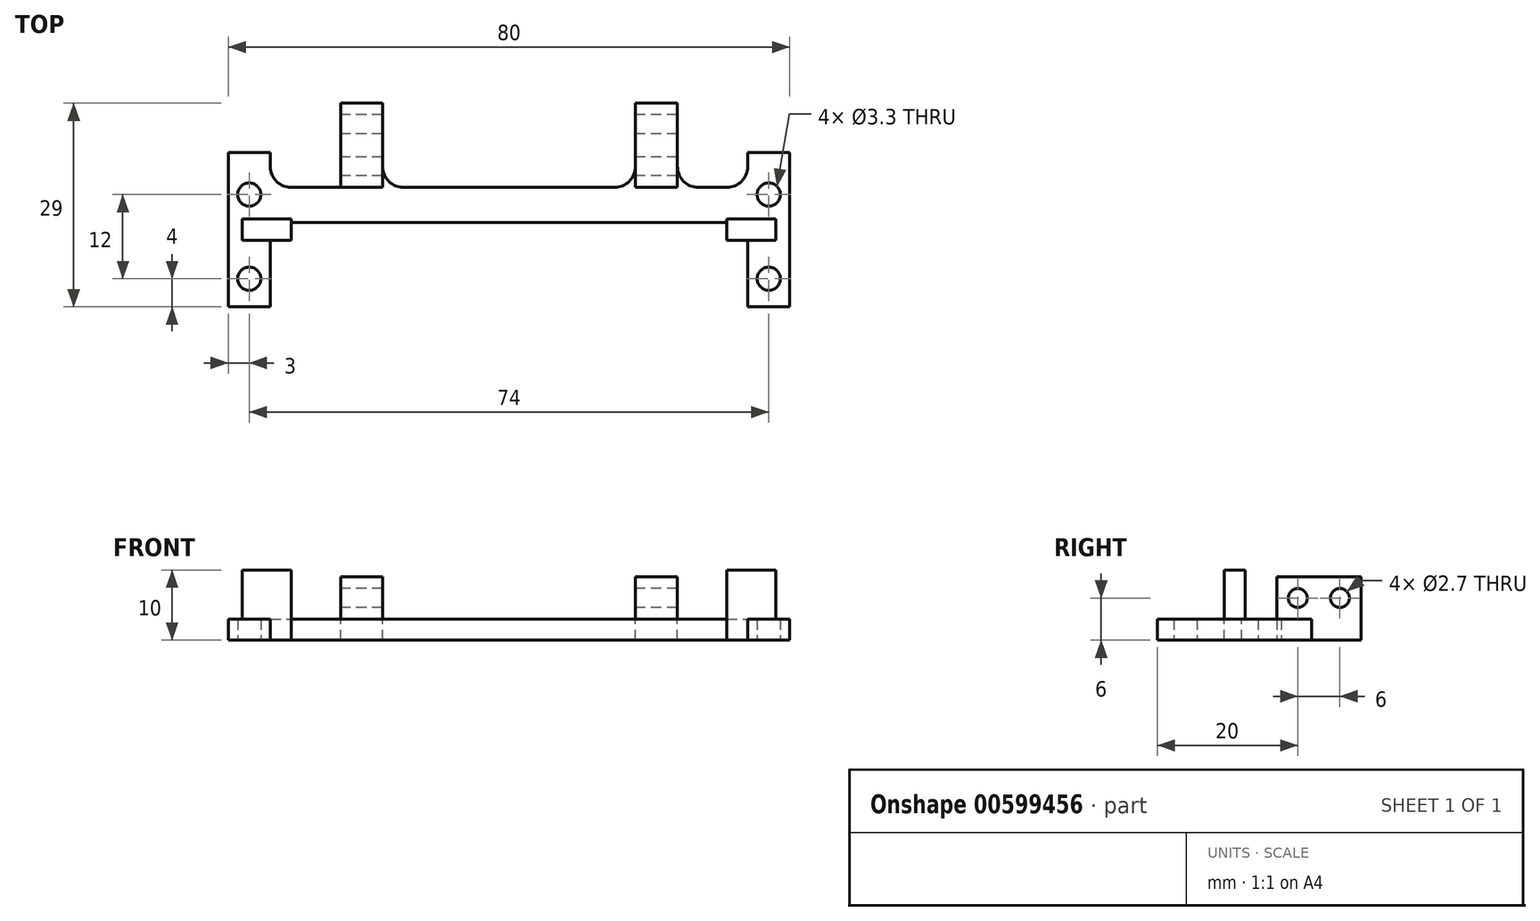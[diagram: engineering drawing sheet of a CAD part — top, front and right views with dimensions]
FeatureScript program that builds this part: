
annotation { "Feature Type Name" : "Feature", "Feature Type Description" : "" }
export const myFeature = defineFeature(function(context is Context, id is Id, definition is map)
    precondition{}
    {
        {
            var Q0;
            Q0=qCreatedBy(makeId("Top.planeOp"),FACE);
            var sketch = newSketch(context, id + "F0", { "sketchPlane" : qUnion([Q0])});
            skLineSegment(sketch, "E0.bottom", {"start": v(-40, 6) * mm, "end": v(-34, 6) * mm});
            skLineSegment(sketch, "E0.top", {"start": v(-34, -4) * mm, "end": v(34, -4) * mm});
            skLineSegment(sketch, "E0.left", {"start": v(-40, 6) * mm, "end": v(-40, -4) * mm});
            skLineSegment(sketch, "E0.right", {"start": v(40, 6) * mm, "end": v(40, -4) * mm});
            skCircle(sketch, "E1", {"center": v(-37, 0) * mm, "radius": 1.65 * mm});
            skCircle(sketch, "E2", {"center": v(37, 0) * mm, "radius": 1.65 * mm});
            skLineSegment(sketch, "E3", {"start": v(34, 6) * mm, "end": v(34, 1) * mm});
            skLineSegment(sketch, "E4", {"start": v(-34, 6) * mm, "end": v(-34, 1) * mm});
            skLineSegment(sketch, "E5", {"start": v(-34, 1) * mm, "end": v(34, 1) * mm});
            skLineSegment(sketch, "E6.trimOffspring", {"start": v(34, 6) * mm, "end": v(40, 6) * mm});
            skLineSegment(sketch, "E7.top", {"start": v(34, -16) * mm, "end": v(40, -16) * mm});
            skLineSegment(sketch, "E7.right", {"start": v(40, -4) * mm, "end": v(40, -16) * mm});
            skLineSegment(sketch, "E8.trimOffspring", {"start": v(34, -4) * mm, "end": v(34, -16) * mm});
            skLineSegment(sketch, "E9.MirrorCS", {"start": v(-34, -4) * mm, "end": v(-34, -16) * mm});
            skLineSegment(sketch, "E10.MirrorCS", {"start": v(-34, -16) * mm, "end": v(-40, -16) * mm});
            skLineSegment(sketch, "E11.MirrorCS", {"start": v(-40, -4) * mm, "end": v(-40, -16) * mm});
            skCircle(sketch, "E12", {"center": v(-37, -12) * mm, "radius": 1.65 * mm});
            skCircle(sketch, "E13.MirrorC", {"center": v(37, -12) * mm, "radius": 1.65 * mm});
            skSolve(sketch);
        }
        {
            var Q0;
            Q0=makeQuery(id+"F0.imprint","IMPRINT",FACE,{"disambiguationData":[TD([[makeQuery(id+"F0.imprint","IMPRINT",EDGE,{"derivedFrom":sQuery(id+"F0.wireOp",EDGE,"E0.bottom")}),-1.0]])]});
            extrude(context, id + "F1", {"entities" : qUnion([Q0]), "depth" : 3 * mm, "offsetDistance" : 25 * mm});
        }
        {
            var Q0;
            Q0=makeQuery(id+"F1.opExtrude","CAP_FACE",FACE,{"disambiguationData":[OSD([sQuery(id+"F0.wireOp",EDGE,"E0.bottom"),sQuery(id+"F0.wireOp",EDGE,"E0.top"),sQuery(id+"F0.wireOp",EDGE,"E0.left"),sQuery(id+"F0.wireOp",EDGE,"E0.right"),sQuery(id+"F0.wireOp",EDGE,"E1"),sQuery(id+"F0.wireOp",EDGE,"E2"),sQuery(id+"F0.wireOp",EDGE,"E3"),sQuery(id+"F0.wireOp",EDGE,"E4"),sQuery(id+"F0.wireOp",EDGE,"E5"),sQuery(id+"F0.wireOp",EDGE,"E6.trimOffspring")])],"isStart":false});
            var sketch = newSketch(context, id + "F2", { "sketchPlane" : qUnion([Q0])});
            skLineSegment(sketch, "E14.bottom", {"start": v(-24, 13) * mm, "end": v(-18, 13) * mm});
            skLineSegment(sketch, "E14.top", {"start": v(-24, -4) * mm, "end": v(-18, -4) * mm});
            skLineSegment(sketch, "E14.left", {"start": v(-24, 13) * mm, "end": v(-24, -4) * mm});
            skLineSegment(sketch, "E14.right", {"start": v(-18, 13) * mm, "end": v(-18, -4) * mm});
            skLineSegment(sketch, "E15.MirrorCS", {"start": v(18, 13) * mm, "end": v(18, -4) * mm});
            skLineSegment(sketch, "E16.MirrorCS", {"start": v(24, 13) * mm, "end": v(18, 13) * mm});
            skLineSegment(sketch, "E17.MirrorCS", {"start": v(24, 13) * mm, "end": v(24, -4) * mm});
            skLineSegment(sketch, "E18.MirrorCS", {"start": v(24, -4) * mm, "end": v(18, -4) * mm});
            skSolve(sketch);
        }
        {
            var Q0;
            {var subQ0=sQuery(id+"F2.wireOp",EDGE,"E14.bottom");Q0=makeQuery(id+"F2.imprint","IMPRINT",FACE,{"disambiguationData":[TD([[makeQuery(id+"F2.imprint","IMPRINT",EDGE,{"derivedFrom":subQ0}),-1.0]])]});}
            var Q1;
            {var subQ0=sQuery(id+"F2.wireOp",EDGE,"E16.MirrorCS");Q1=makeQuery(id+"F2.imprint","IMPRINT",FACE,{"disambiguationData":[TD([[makeQuery(id+"F2.imprint","IMPRINT",EDGE,{"derivedFrom":subQ0}),1.0]])]});}
            extrude(context, id + "F3", {"entities" : qUnion([Q0, Q1]), "operationType" : NewBodyOperationType.ADD, "oppositeDirection" : true, "depth" : 3 * mm, "offsetDistance" : 25 * mm});
        }
        {
            var Q0;
            {var subQ0=sQuery(id+"F0.wireOp",EDGE,"E5");Q0=makeQuery(id+"F3.boolean.opBoolean","MERGE",FACE,{"derivedFrom":[makeQuery(id+"F1.opExtrude","CAP_FACE",FACE,{"disambiguationData":[OSD([sQuery(id+"F0.wireOp",EDGE,"E0.bottom"),sQuery(id+"F0.wireOp",EDGE,"E0.top"),sQuery(id+"F0.wireOp",EDGE,"E0.left"),sQuery(id+"F0.wireOp",EDGE,"E0.right"),sQuery(id+"F0.wireOp",EDGE,"E1"),sQuery(id+"F0.wireOp",EDGE,"E2"),sQuery(id+"F0.wireOp",EDGE,"E3"),sQuery(id+"F0.wireOp",EDGE,"E4"),subQ0,sQuery(id+"F0.wireOp",EDGE,"E6.trimOffspring")])],"isStart":false}),makeQuery(id+"F3.opExtrude","CAP_FACE",FACE,{"disambiguationData":[OSD([subQ0,sQuery(id+"F2.wireOp",EDGE,"E14.bottom"),sQuery(id+"F2.wireOp",EDGE,"E14.left"),sQuery(id+"F2.wireOp",EDGE,"E14.right")])],"isStart":true}),makeQuery(id+"F3.opExtrude","CAP_FACE",FACE,{"disambiguationData":[OSD([subQ0,sQuery(id+"F2.wireOp",EDGE,"E15.MirrorCS"),sQuery(id+"F2.wireOp",EDGE,"E16.MirrorCS"),sQuery(id+"F2.wireOp",EDGE,"E17.MirrorCS")])],"isStart":true})]});}
            var sketch = newSketch(context, id + "F4", { "sketchPlane" : qUnion([Q0])});
            skPoint(sketch, "E19.left.end.orphan", {"position": v(-24, 7) * mm});
            skPoint(sketch, "E19.bottom.start.orphan", {"position": v(-24, 13) * mm});
            skPoint(sketch, "E19.right.end.orphan", {"position": v(-18, 7) * mm});
            skPoint(sketch, "E19.right.start.orphan", {"position": v(-18, 13) * mm});
            skPoint(sketch, "E20.MirrorCS.end.orphan", {"position": v(18, 7) * mm});
            skPoint(sketch, "E20.MirrorCS.start.orphan", {"position": v(18, 13) * mm});
            skPoint(sketch, "E21.MirrorCS.start.orphan", {"position": v(24, 13) * mm});
            skPoint(sketch, "E22.MirrorCS.end.orphan", {"position": v(24, 7) * mm});
            skLineSegment(sketch, "E23.bottom", {"start": v(-24, 13) * mm, "end": v(-18, 13) * mm});
            skLineSegment(sketch, "E23.top", {"start": v(-24, 1) * mm, "end": v(-18, 1) * mm});
            skLineSegment(sketch, "E23.left", {"start": v(-24, 13) * mm, "end": v(-24, 1) * mm});
            skLineSegment(sketch, "E23.right", {"start": v(-18, 13) * mm, "end": v(-18, 1) * mm});
            skLineSegment(sketch, "E24.bottom", {"start": v(18, 13) * mm, "end": v(18, 13) * mm});
            skLineSegment(sketch, "E24.top", {"start": v(18, 1) * mm, "end": v(18, 1) * mm});
            skLineSegment(sketch, "E24.left", {"start": v(18, 13) * mm, "end": v(18, 1) * mm});
            skLineSegment(sketch, "E24.right", {"start": v(18, 13) * mm, "end": v(18, 1) * mm});
            skLineSegment(sketch, "E25.bottom", {"start": v(24, 1) * mm, "end": v(18, 1) * mm});
            skLineSegment(sketch, "E25.top", {"start": v(24, 13) * mm, "end": v(18, 13) * mm});
            skLineSegment(sketch, "E25.left", {"start": v(24, 1) * mm, "end": v(24, 13) * mm});
            skLineSegment(sketch, "E25.right", {"start": v(18, 1) * mm, "end": v(18, 13) * mm});
            skSolve(sketch);
        }
        {
            var Q0;
            {var subQ0=sQuery(id+"F0.wireOp",EDGE,"E5");Q0=makeQuery(id+"F3.boolean.opBoolean","MERGE",FACE,{"derivedFrom":[makeQuery(id+"F1.opExtrude","CAP_FACE",FACE,{"disambiguationData":[OSD([sQuery(id+"F0.wireOp",EDGE,"E0.bottom"),sQuery(id+"F0.wireOp",EDGE,"E0.top"),sQuery(id+"F0.wireOp",EDGE,"E0.left"),sQuery(id+"F0.wireOp",EDGE,"E0.right"),sQuery(id+"F0.wireOp",EDGE,"E1"),sQuery(id+"F0.wireOp",EDGE,"E2"),sQuery(id+"F0.wireOp",EDGE,"E3"),sQuery(id+"F0.wireOp",EDGE,"E4"),subQ0,sQuery(id+"F0.wireOp",EDGE,"E6.trimOffspring"),sQuery(id+"F0.wireOp",EDGE,"E7.top"),sQuery(id+"F0.wireOp",EDGE,"E7.right"),sQuery(id+"F0.wireOp",EDGE,"E8.trimOffspring"),sQuery(id+"F0.wireOp",EDGE,"E9.MirrorCS"),sQuery(id+"F0.wireOp",EDGE,"E10.MirrorCS"),sQuery(id+"F0.wireOp",EDGE,"E11.MirrorCS")])],"isStart":false}),makeQuery(id+"F3.opExtrude","CAP_FACE",FACE,{"disambiguationData":[OSD([subQ0,sQuery(id+"F2.wireOp",EDGE,"E14.bottom"),sQuery(id+"F2.wireOp",EDGE,"E14.left"),sQuery(id+"F2.wireOp",EDGE,"E14.right")])],"isStart":true}),makeQuery(id+"F3.opExtrude","CAP_FACE",FACE,{"disambiguationData":[OSD([subQ0,sQuery(id+"F2.wireOp",EDGE,"E15.MirrorCS"),sQuery(id+"F2.wireOp",EDGE,"E16.MirrorCS"),sQuery(id+"F2.wireOp",EDGE,"E17.MirrorCS")])],"isStart":true})]});}
            var sketch = newSketch(context, id + "F5", { "sketchPlane" : qUnion([Q0])});
            skLineSegment(sketch, "E26.bottom", {"start": v(-38, -3.5) * mm, "end": v(-31, -3.5) * mm});
            skLineSegment(sketch, "E26.top", {"start": v(-38, -6.5) * mm, "end": v(-31, -6.5) * mm});
            skLineSegment(sketch, "E26.left", {"start": v(-38, -3.5) * mm, "end": v(-38, -6.5) * mm});
            skLineSegment(sketch, "E26.right", {"start": v(-31, -3.5) * mm, "end": v(-31, -6.5) * mm});
            skLineSegment(sketch, "E27.MirrorCS", {"start": v(31, -3.5) * mm, "end": v(31, -6.5) * mm});
            skLineSegment(sketch, "E28.MirrorCS", {"start": v(38, -3.5) * mm, "end": v(31, -3.5) * mm});
            skLineSegment(sketch, "E29.MirrorCS", {"start": v(38, -3.5) * mm, "end": v(38, -6.5) * mm});
            skLineSegment(sketch, "E30.MirrorCS", {"start": v(38, -6.5) * mm, "end": v(31, -6.5) * mm});
            skLineSegment(sketch, "E31", {"start": v(-31, -3.5) * mm, "end": v(-38, -3.5) * mm});
            skSolve(sketch);
        }
        {
            var Q0;
            {var subQ0=sQuery(id+"F5.wireOp",EDGE,"E26.left");Q0=makeQuery(id+"F5.imprint","IMPRINT",FACE,{"disambiguationData":[TD([[makeQuery(id+"F5.imprint","IMPRINT",EDGE,{"derivedFrom":subQ0}),1.0]])]});}
            var Q1;
            {var subQ0=sQuery(id+"F5.wireOp",EDGE,"E26.right");Q1=makeQuery(id+"F5.imprint","IMPRINT",FACE,{"disambiguationData":[TD([[makeQuery(id+"F5.imprint","IMPRINT",EDGE,{"derivedFrom":subQ0}),-1.0]])]});}
            var Q2;
            {var subQ0=sQuery(id+"F5.wireOp",EDGE,"E27.MirrorCS");Q2=makeQuery(id+"F5.imprint","IMPRINT",FACE,{"disambiguationData":[TD([[makeQuery(id+"F5.imprint","IMPRINT",EDGE,{"derivedFrom":subQ0}),1.0]])]});}
            var Q3;
            {var subQ0=sQuery(id+"F5.wireOp",EDGE,"E29.MirrorCS");Q3=makeQuery(id+"F5.imprint","IMPRINT",FACE,{"disambiguationData":[TD([[makeQuery(id+"F5.imprint","IMPRINT",EDGE,{"derivedFrom":subQ0}),-1.0]])]});}
            extrude(context, id + "F6", {"entities" : qUnion([Q0, Q1, Q2, Q3]), "operationType" : NewBodyOperationType.ADD, "depth" : 7 * mm, "offsetDistance" : 25 * mm});
        }
        {
            var Q0;
            Q0=makeQuery(id+"F6.opExtrude","CAP_FACE",FACE,{"disambiguationData":[OSD([sQuery(id+"F5.wireOp",EDGE,"E27.MirrorCS"),sQuery(id+"F5.wireOp",EDGE,"E28.MirrorCS"),sQuery(id+"F5.wireOp",EDGE,"E29.MirrorCS"),sQuery(id+"F5.wireOp",EDGE,"E30.MirrorCS")])],"isStart":true});
            var Q1;
            Q1=makeQuery(id+"F6.opExtrude","CAP_FACE",FACE,{"disambiguationData":[OSD([sQuery(id+"F5.wireOp",EDGE,"E26.top"),sQuery(id+"F5.wireOp",EDGE,"E26.left"),sQuery(id+"F5.wireOp",EDGE,"E26.right"),sQuery(id+"F5.wireOp",EDGE,"E31")])],"isStart":true});
            extrude(context, id + "F7", {"entities" : qUnion([Q0, Q1]), "operationType" : NewBodyOperationType.ADD, "depth" : 3 * mm, "offsetDistance" : 25 * mm});
        }
        {
            var Q0;
            Q0=makeQuery(id+"F4.imprint","IMPRINT",FACE,{"disambiguationData":[TD([[makeQuery(id+"F4.imprint","IMPRINT",EDGE,{"derivedFrom":sQuery(id+"F4.wireOp",EDGE,"E23.bottom")}),-1.0]])]});
            var Q1;
            Q1=makeQuery(id+"F4.imprint","IMPRINT",FACE,{"disambiguationData":[TD([[makeQuery(id+"F4.imprint","IMPRINT",EDGE,{"derivedFrom":sQuery(id+"F4.wireOp",EDGE,"E25.bottom")}),-1.0]])]});
            extrude(context, id + "F8", {"entities" : qUnion([Q0, Q1]), "operationType" : NewBodyOperationType.ADD, "depth" : 3 * mm, "offsetDistance" : 25 * mm});
        }
        {
            var Q0;
            Q0=makeQuery(id+"F8.opExtrude","CAP_FACE",FACE,{"disambiguationData":[OSD([sQuery(id+"F4.wireOp",EDGE,"E23.bottom"),sQuery(id+"F4.wireOp",EDGE,"E23.top"),sQuery(id+"F4.wireOp",EDGE,"E23.left"),sQuery(id+"F4.wireOp",EDGE,"E23.right")])],"isStart":false});
            var sketch = newSketch(context, id + "F9", { "sketchPlane" : qUnion([Q0])});
            skLineSegment(sketch, "E32.bottom", {"start": v(-24, 1) * mm, "end": v(-18, 1) * mm});
            skLineSegment(sketch, "E32.top", {"start": v(-24, 7) * mm, "end": v(-18, 7) * mm});
            skLineSegment(sketch, "E32.left", {"start": v(-24, 1) * mm, "end": v(-24, 7) * mm});
            skLineSegment(sketch, "E32.right", {"start": v(-18, 1) * mm, "end": v(-18, 7) * mm});
            skLineSegment(sketch, "E33.MirrorCS", {"start": v(24, 7) * mm, "end": v(18, 7) * mm});
            skLineSegment(sketch, "E34.MirrorCS", {"start": v(24, 1) * mm, "end": v(24, 7) * mm});
            skLineSegment(sketch, "E35.MirrorCS", {"start": v(24, 1) * mm, "end": v(18, 1) * mm});
            skLineSegment(sketch, "E36.MirrorCS", {"start": v(18, 1) * mm, "end": v(18, 7) * mm});
            skSolve(sketch);
        }
        {
            var Q0;
            Q0=makeQuery(id+"F9.imprint","IMPRINT",FACE,{"disambiguationData":[TD([[makeQuery(id+"F9.imprint","IMPRINT",EDGE,{"derivedFrom":sQuery(id+"F9.wireOp",EDGE,"E32.bottom")}),1.0]])]});
            var Q1;
            Q1=makeQuery(id+"F9.imprint","IMPRINT",FACE,{"disambiguationData":[TD([[makeQuery(id+"F9.imprint","IMPRINT",EDGE,{"derivedFrom":sQuery(id+"F9.wireOp",EDGE,"E33.MirrorCS")}),1.0]])]});
            extrude(context, id + "F10", {"entities" : qUnion([Q0, Q1]), "operationType" : NewBodyOperationType.ADD, "depth" : 3 * mm, "offsetDistance" : 25 * mm});
        }
        {
            var Q0;
            Q0=makeQuery(id+"F3.opExtrude","SWEPT_EDGE",EDGE,{"disambiguationData":[OSD([sQuery(id+"F0.wireOp",EDGE,"E5"),sQuery(id+"F2.wireOp",EDGE,"E14.left")])]});
            var Q1;
            Q1=makeQuery(id+"F3.opExtrude","SWEPT_EDGE",EDGE,{"disambiguationData":[OSD([sQuery(id+"F0.wireOp",EDGE,"E5"),sQuery(id+"F2.wireOp",EDGE,"E15.MirrorCS")])]});
            var Q2;
            Q2=makeQuery(id+"F3.opExtrude","SWEPT_EDGE",EDGE,{"disambiguationData":[OSD([sQuery(id+"F0.wireOp",EDGE,"E5"),sQuery(id+"F2.wireOp",EDGE,"E14.right")])]});
            var Q3;
            Q3=makeQuery(id+"F3.opExtrude","SWEPT_EDGE",EDGE,{"disambiguationData":[OSD([sQuery(id+"F0.wireOp",EDGE,"E5"),sQuery(id+"F2.wireOp",EDGE,"E17.MirrorCS")])]});
            var Q4;
            Q4=makeQuery(id+"F1.opExtrude","SWEPT_EDGE",EDGE,{"disambiguationData":[OSD([sQuery(id+"F0.wireOp",EDGE,"E4"),sQuery(id+"F0.wireOp",EDGE,"E5")])]});
            var Q5;
            Q5=makeQuery(id+"F1.opExtrude","SWEPT_EDGE",EDGE,{"disambiguationData":[OSD([sQuery(id+"F0.wireOp",EDGE,"E3"),sQuery(id+"F0.wireOp",EDGE,"E5")])]});
            var Q6;
            {var subQ0=sQuery(id+"F5.wireOp",EDGE,"E30.MirrorCS");var subQ1=sQuery(id+"F5.wireOp",EDGE,"E29.MirrorCS");var subQ2=sQuery(id+"F5.wireOp",EDGE,"E28.MirrorCS");var subQ3=sQuery(id+"F5.wireOp",EDGE,"E27.MirrorCS");var subQ4=sQuery(id+"F2.wireOp",EDGE,"E17.MirrorCS");var subQ5=sQuery(id+"F2.wireOp",EDGE,"E16.MirrorCS");var subQ6=sQuery(id+"F2.wireOp",EDGE,"E15.MirrorCS");var subQ7=sQuery(id+"F0.wireOp",EDGE,"E5");var subQ8=sQuery(id+"F2.wireOp",EDGE,"E14.right");var subQ9=sQuery(id+"F2.wireOp",EDGE,"E14.left");var subQ10=sQuery(id+"F2.wireOp",EDGE,"E14.bottom");var subQ11=sQuery(id+"F0.wireOp",EDGE,"E13.MirrorC");var subQ12=sQuery(id+"F0.wireOp",EDGE,"E12");var subQ13=sQuery(id+"F0.wireOp",EDGE,"E11.MirrorCS");var subQ14=sQuery(id+"F0.wireOp",EDGE,"E10.MirrorCS");var subQ15=sQuery(id+"F0.wireOp",EDGE,"E9.MirrorCS");var subQ16=sQuery(id+"F0.wireOp",EDGE,"E8.trimOffspring");var subQ17=sQuery(id+"F0.wireOp",EDGE,"E7.right");var subQ18=sQuery(id+"F0.wireOp",EDGE,"E7.top");var subQ19=sQuery(id+"F0.wireOp",EDGE,"E6.trimOffspring");var subQ20=sQuery(id+"F0.wireOp",EDGE,"E4");var subQ21=sQuery(id+"F0.wireOp",EDGE,"E3");var subQ22=sQuery(id+"F0.wireOp",EDGE,"E2");var subQ23=sQuery(id+"F0.wireOp",EDGE,"E1");var subQ24=sQuery(id+"F0.wireOp",EDGE,"E0.right");var subQ25=sQuery(id+"F0.wireOp",EDGE,"E0.left");var subQ26=sQuery(id+"F0.wireOp",EDGE,"E0.top");var subQ27=sQuery(id+"F0.wireOp",EDGE,"E0.bottom");Q6=makeQuery(id+"F7.opExtrude","SWEPT_EDGE",EDGE,{"disambiguationData":[OSD([subQ27,subQ26,subQ25,subQ24,subQ23,subQ22,subQ21,subQ20,subQ7,subQ19,subQ18,subQ17,subQ16,subQ15,subQ14,subQ13,subQ12,subQ11,subQ10,subQ9,subQ8,subQ6,subQ5,subQ4,subQ3,subQ2,subQ1,subQ0]),TDD([makeQuery(id+"F6.boolean.opBoolean","TWEAK_VERTEX",VERTEX,{"derivedFrom":[makeQuery(id+"F1.opExtrude","SWEPT_FACE",FACE,{"disambiguationData":[OSD([subQ26])]}),makeQuery(id+"F3.boolean.opBoolean","MERGE",FACE,{"derivedFrom":[makeQuery(id+"F1.opExtrude","CAP_FACE",FACE,{"disambiguationData":[OSD([subQ27,subQ26,subQ25,subQ24,subQ23,subQ22,subQ21,subQ20,subQ7,subQ19,subQ18,subQ17,subQ16,subQ15,subQ14,subQ13,subQ12,subQ11])],"isStart":false}),makeQuery(id+"F3.opExtrude","CAP_FACE",FACE,{"disambiguationData":[OSD([subQ7,subQ10,subQ9,subQ8])],"isStart":true}),makeQuery(id+"F3.opExtrude","CAP_FACE",FACE,{"disambiguationData":[OSD([subQ7,subQ6,subQ5,subQ4])],"isStart":true})]}),makeQuery(id+"F6.opExtrude","SWEPT_FACE",FACE,{"disambiguationData":[OSD([subQ3])]}),makeQuery(id+"F6.opExtrude","CAP_FACE",FACE,{"disambiguationData":[OSD([subQ3,subQ2,subQ1,subQ0])],"isStart":true})]})])]});}
            var Q7;
            {var subQ0=sQuery(id+"F5.wireOp",EDGE,"E26.right");var subQ1=sQuery(id+"F5.wireOp",EDGE,"E31");var subQ2=sQuery(id+"F5.wireOp",EDGE,"E26.left");var subQ3=sQuery(id+"F5.wireOp",EDGE,"E26.top");var subQ4=sQuery(id+"F2.wireOp",EDGE,"E17.MirrorCS");var subQ5=sQuery(id+"F2.wireOp",EDGE,"E16.MirrorCS");var subQ6=sQuery(id+"F2.wireOp",EDGE,"E15.MirrorCS");var subQ7=sQuery(id+"F0.wireOp",EDGE,"E5");var subQ8=sQuery(id+"F2.wireOp",EDGE,"E14.right");var subQ9=sQuery(id+"F2.wireOp",EDGE,"E14.left");var subQ10=sQuery(id+"F2.wireOp",EDGE,"E14.bottom");var subQ11=sQuery(id+"F0.wireOp",EDGE,"E13.MirrorC");var subQ12=sQuery(id+"F0.wireOp",EDGE,"E12");var subQ13=sQuery(id+"F0.wireOp",EDGE,"E11.MirrorCS");var subQ14=sQuery(id+"F0.wireOp",EDGE,"E10.MirrorCS");var subQ15=sQuery(id+"F0.wireOp",EDGE,"E9.MirrorCS");var subQ16=sQuery(id+"F0.wireOp",EDGE,"E8.trimOffspring");var subQ17=sQuery(id+"F0.wireOp",EDGE,"E7.right");var subQ18=sQuery(id+"F0.wireOp",EDGE,"E7.top");var subQ19=sQuery(id+"F0.wireOp",EDGE,"E6.trimOffspring");var subQ20=sQuery(id+"F0.wireOp",EDGE,"E4");var subQ21=sQuery(id+"F0.wireOp",EDGE,"E3");var subQ22=sQuery(id+"F0.wireOp",EDGE,"E2");var subQ23=sQuery(id+"F0.wireOp",EDGE,"E1");var subQ24=sQuery(id+"F0.wireOp",EDGE,"E0.right");var subQ25=sQuery(id+"F0.wireOp",EDGE,"E0.left");var subQ26=sQuery(id+"F0.wireOp",EDGE,"E0.top");var subQ27=sQuery(id+"F0.wireOp",EDGE,"E0.bottom");Q7=makeQuery(id+"F7.opExtrude","SWEPT_EDGE",EDGE,{"disambiguationData":[OSD([subQ27,subQ26,subQ25,subQ24,subQ23,subQ22,subQ21,subQ20,subQ7,subQ19,subQ18,subQ17,subQ16,subQ15,subQ14,subQ13,subQ12,subQ11,subQ10,subQ9,subQ8,subQ6,subQ5,subQ4,subQ3,subQ2,subQ0,subQ1]),TDD([makeQuery(id+"F6.boolean.opBoolean","TWEAK_VERTEX",VERTEX,{"derivedFrom":[makeQuery(id+"F1.opExtrude","SWEPT_FACE",FACE,{"disambiguationData":[OSD([subQ26])]}),makeQuery(id+"F3.boolean.opBoolean","MERGE",FACE,{"derivedFrom":[makeQuery(id+"F1.opExtrude","CAP_FACE",FACE,{"disambiguationData":[OSD([subQ27,subQ26,subQ25,subQ24,subQ23,subQ22,subQ21,subQ20,subQ7,subQ19,subQ18,subQ17,subQ16,subQ15,subQ14,subQ13,subQ12,subQ11])],"isStart":false}),makeQuery(id+"F3.opExtrude","CAP_FACE",FACE,{"disambiguationData":[OSD([subQ7,subQ10,subQ9,subQ8])],"isStart":true}),makeQuery(id+"F3.opExtrude","CAP_FACE",FACE,{"disambiguationData":[OSD([subQ7,subQ6,subQ5,subQ4])],"isStart":true})]}),makeQuery(id+"F6.opExtrude","CAP_FACE",FACE,{"disambiguationData":[OSD([subQ3,subQ2,subQ0,subQ1])],"isStart":true}),makeQuery(id+"F6.opExtrude","SWEPT_FACE",FACE,{"disambiguationData":[OSD([subQ0])]})]})])]});}
            var Q8;
            {var subQ0=sQuery(id+"F5.wireOp",EDGE,"E31");var subQ1=sQuery(id+"F5.wireOp",EDGE,"E26.right");var subQ2=sQuery(id+"F5.wireOp",EDGE,"E26.left");var subQ3=sQuery(id+"F5.wireOp",EDGE,"E26.top");var subQ4=sQuery(id+"F2.wireOp",EDGE,"E17.MirrorCS");var subQ5=sQuery(id+"F2.wireOp",EDGE,"E16.MirrorCS");var subQ6=sQuery(id+"F2.wireOp",EDGE,"E15.MirrorCS");var subQ7=sQuery(id+"F0.wireOp",EDGE,"E5");var subQ8=sQuery(id+"F2.wireOp",EDGE,"E14.right");var subQ9=sQuery(id+"F2.wireOp",EDGE,"E14.left");var subQ10=sQuery(id+"F2.wireOp",EDGE,"E14.bottom");var subQ11=sQuery(id+"F0.wireOp",EDGE,"E13.MirrorC");var subQ12=sQuery(id+"F0.wireOp",EDGE,"E12");var subQ13=sQuery(id+"F0.wireOp",EDGE,"E11.MirrorCS");var subQ14=sQuery(id+"F0.wireOp",EDGE,"E10.MirrorCS");var subQ15=sQuery(id+"F0.wireOp",EDGE,"E9.MirrorCS");var subQ16=sQuery(id+"F0.wireOp",EDGE,"E8.trimOffspring");var subQ17=sQuery(id+"F0.wireOp",EDGE,"E7.right");var subQ18=sQuery(id+"F0.wireOp",EDGE,"E7.top");var subQ19=sQuery(id+"F0.wireOp",EDGE,"E6.trimOffspring");var subQ20=sQuery(id+"F0.wireOp",EDGE,"E4");var subQ21=sQuery(id+"F0.wireOp",EDGE,"E3");var subQ22=sQuery(id+"F0.wireOp",EDGE,"E2");var subQ23=sQuery(id+"F0.wireOp",EDGE,"E1");var subQ24=sQuery(id+"F0.wireOp",EDGE,"E0.right");var subQ25=sQuery(id+"F0.wireOp",EDGE,"E0.left");var subQ26=sQuery(id+"F0.wireOp",EDGE,"E0.top");var subQ27=sQuery(id+"F0.wireOp",EDGE,"E0.bottom");Q8=makeQuery(id+"F7.opExtrude","SWEPT_EDGE",EDGE,{"disambiguationData":[OSD([subQ27,subQ26,subQ25,subQ24,subQ23,subQ22,subQ21,subQ20,subQ7,subQ19,subQ18,subQ17,subQ16,subQ15,subQ14,subQ13,subQ12,subQ11,subQ10,subQ9,subQ8,subQ6,subQ5,subQ4,subQ3,subQ2,subQ1,subQ0]),TDD([makeQuery(id+"F6.boolean.opBoolean","TWEAK_VERTEX",VERTEX,{"derivedFrom":[makeQuery(id+"F1.opExtrude","SWEPT_FACE",FACE,{"disambiguationData":[OSD([subQ15])]}),makeQuery(id+"F3.boolean.opBoolean","MERGE",FACE,{"derivedFrom":[makeQuery(id+"F1.opExtrude","CAP_FACE",FACE,{"disambiguationData":[OSD([subQ27,subQ26,subQ25,subQ24,subQ23,subQ22,subQ21,subQ20,subQ7,subQ19,subQ18,subQ17,subQ16,subQ15,subQ14,subQ13,subQ12,subQ11])],"isStart":false}),makeQuery(id+"F3.opExtrude","CAP_FACE",FACE,{"disambiguationData":[OSD([subQ7,subQ10,subQ9,subQ8])],"isStart":true}),makeQuery(id+"F3.opExtrude","CAP_FACE",FACE,{"disambiguationData":[OSD([subQ7,subQ6,subQ5,subQ4])],"isStart":true})]}),makeQuery(id+"F6.opExtrude","SWEPT_FACE",FACE,{"disambiguationData":[OSD([subQ3])]}),makeQuery(id+"F6.opExtrude","CAP_FACE",FACE,{"disambiguationData":[OSD([subQ3,subQ2,subQ1,subQ0])],"isStart":true})]})])]});}
            var Q9;
            {var subQ0=sQuery(id+"F5.wireOp",EDGE,"E30.MirrorCS");var subQ1=sQuery(id+"F5.wireOp",EDGE,"E29.MirrorCS");var subQ2=sQuery(id+"F5.wireOp",EDGE,"E28.MirrorCS");var subQ3=sQuery(id+"F5.wireOp",EDGE,"E27.MirrorCS");var subQ4=sQuery(id+"F2.wireOp",EDGE,"E17.MirrorCS");var subQ5=sQuery(id+"F2.wireOp",EDGE,"E16.MirrorCS");var subQ6=sQuery(id+"F2.wireOp",EDGE,"E15.MirrorCS");var subQ7=sQuery(id+"F0.wireOp",EDGE,"E5");var subQ8=sQuery(id+"F2.wireOp",EDGE,"E14.right");var subQ9=sQuery(id+"F2.wireOp",EDGE,"E14.left");var subQ10=sQuery(id+"F2.wireOp",EDGE,"E14.bottom");var subQ11=sQuery(id+"F0.wireOp",EDGE,"E13.MirrorC");var subQ12=sQuery(id+"F0.wireOp",EDGE,"E12");var subQ13=sQuery(id+"F0.wireOp",EDGE,"E11.MirrorCS");var subQ14=sQuery(id+"F0.wireOp",EDGE,"E10.MirrorCS");var subQ15=sQuery(id+"F0.wireOp",EDGE,"E9.MirrorCS");var subQ16=sQuery(id+"F0.wireOp",EDGE,"E8.trimOffspring");var subQ17=sQuery(id+"F0.wireOp",EDGE,"E7.right");var subQ18=sQuery(id+"F0.wireOp",EDGE,"E7.top");var subQ19=sQuery(id+"F0.wireOp",EDGE,"E6.trimOffspring");var subQ20=sQuery(id+"F0.wireOp",EDGE,"E4");var subQ21=sQuery(id+"F0.wireOp",EDGE,"E3");var subQ22=sQuery(id+"F0.wireOp",EDGE,"E2");var subQ23=sQuery(id+"F0.wireOp",EDGE,"E1");var subQ24=sQuery(id+"F0.wireOp",EDGE,"E0.right");var subQ25=sQuery(id+"F0.wireOp",EDGE,"E0.left");var subQ26=sQuery(id+"F0.wireOp",EDGE,"E0.top");var subQ27=sQuery(id+"F0.wireOp",EDGE,"E0.bottom");Q9=makeQuery(id+"F7.opExtrude","SWEPT_EDGE",EDGE,{"disambiguationData":[OSD([subQ27,subQ26,subQ25,subQ24,subQ23,subQ22,subQ21,subQ20,subQ7,subQ19,subQ18,subQ17,subQ16,subQ15,subQ14,subQ13,subQ12,subQ11,subQ10,subQ9,subQ8,subQ6,subQ5,subQ4,subQ3,subQ2,subQ1,subQ0]),TDD([makeQuery(id+"F6.boolean.opBoolean","TWEAK_VERTEX",VERTEX,{"derivedFrom":[makeQuery(id+"F1.opExtrude","SWEPT_FACE",FACE,{"disambiguationData":[OSD([subQ16])]}),makeQuery(id+"F3.boolean.opBoolean","MERGE",FACE,{"derivedFrom":[makeQuery(id+"F1.opExtrude","CAP_FACE",FACE,{"disambiguationData":[OSD([subQ27,subQ26,subQ25,subQ24,subQ23,subQ22,subQ21,subQ20,subQ7,subQ19,subQ18,subQ17,subQ16,subQ15,subQ14,subQ13,subQ12,subQ11])],"isStart":false}),makeQuery(id+"F3.opExtrude","CAP_FACE",FACE,{"disambiguationData":[OSD([subQ7,subQ10,subQ9,subQ8])],"isStart":true}),makeQuery(id+"F3.opExtrude","CAP_FACE",FACE,{"disambiguationData":[OSD([subQ7,subQ6,subQ5,subQ4])],"isStart":true})]}),makeQuery(id+"F6.opExtrude","CAP_FACE",FACE,{"disambiguationData":[OSD([subQ3,subQ2,subQ1,subQ0])],"isStart":true}),makeQuery(id+"F6.opExtrude","SWEPT_FACE",FACE,{"disambiguationData":[OSD([subQ0])]})]})])]});}
            fillet(context, id + "F11", {"entities" : qUnion([Q0, Q1, Q2, Q3, Q4, Q5, Q6, Q7, Q8, Q9]), "radius" : 3 * mm, "tangentPropagation" : true, "allowEdgeOverflow" : false});
        }
        {
            var Q0;
            Q0=makeQuery(id+"F10.boolean.opBoolean","MERGE",FACE,{"derivedFrom":[makeQuery(id+"F8.boolean.opBoolean","MERGE",FACE,{"derivedFrom":[makeQuery(id+"F3.opExtrude","SWEPT_FACE",FACE,{"disambiguationData":[OSD([sQuery(id+"F2.wireOp",EDGE,"E14.left")])]}),makeQuery(id+"F8.opExtrude","SWEPT_FACE",FACE,{"disambiguationData":[OSD([sQuery(id+"F4.wireOp",EDGE,"E23.left")])]})]}),makeQuery(id+"F10.opExtrude","SWEPT_FACE",FACE,{"disambiguationData":[OSD([sQuery(id+"F9.wireOp",EDGE,"E32.left")])]})]});
            var sketch = newSketch(context, id + "F12", { "sketchPlane" : qUnion([Q0])});
            skCircle(sketch, "E37", {"center": v(-4, 6) * mm, "radius": 1.35 * mm});
            skPoint(sketch, "E38.center.orphan", {"position": v(-10, 3) * mm});
            skSolve(sketch);
        }
        {
            var Q0;
            Q0=makeQuery(id+"F12.imprint","IMPRINT",FACE,{"disambiguationData":[TD([[makeQuery(id+"F12.imprint","IMPRINT",EDGE,{"derivedFrom":sQuery(id+"F12.wireOp",EDGE,"E38")}),1.0]])]});
            var Q1;
            Q1=makeQuery(id+"F12.imprint","IMPRINT",FACE,{"disambiguationData":[TD([[makeQuery(id+"F12.imprint","IMPRINT",EDGE,{"derivedFrom":sQuery(id+"F12.wireOp",EDGE,"E37")}),1.0]])]});
            extrude(context, id + "F13", {"entities" : qUnion([Q0, Q1]), "operationType" : NewBodyOperationType.REMOVE, "endBound" : BoundingType.THROUGH_ALL, "oppositeDirection" : true, "depth" : 25 * mm, "offsetDistance" : 25 * mm});
        }
        {
            var Q0;
            Q0=makeQuery(id+"F8.opExtrude","CAP_FACE",FACE,{"disambiguationData":[OSD([sQuery(id+"F4.wireOp",EDGE,"E25.bottom"),sQuery(id+"F4.wireOp",EDGE,"E25.top"),sQuery(id+"F4.wireOp",EDGE,"E25.left"),sQuery(id+"F4.wireOp",EDGE,"E25.right")])],"isStart":false});
            var Q1;
            Q1=makeQuery(id+"F8.opExtrude","CAP_FACE",FACE,{"disambiguationData":[OSD([sQuery(id+"F4.wireOp",EDGE,"E23.bottom"),sQuery(id+"F4.wireOp",EDGE,"E23.top"),sQuery(id+"F4.wireOp",EDGE,"E23.left"),sQuery(id+"F4.wireOp",EDGE,"E23.right")])],"isStart":false});
            extrude(context, id + "F14", {"entities" : qUnion([Q0, Q1]), "operationType" : NewBodyOperationType.ADD, "depth" : 3 * mm, "offsetDistance" : 25 * mm});
        }
        {
            var Q0;
            {var subQ0=sQuery(id+"F4.wireOp",EDGE,"E23.left");Q0=makeQuery(id+"F14.boolean.opBoolean","MERGE",FACE,{"derivedFrom":[makeQuery(id+"F10.boolean.opBoolean","MERGE",FACE,{"derivedFrom":[makeQuery(id+"F8.boolean.opBoolean","MERGE",FACE,{"derivedFrom":[makeQuery(id+"F3.opExtrude","SWEPT_FACE",FACE,{"disambiguationData":[OSD([sQuery(id+"F2.wireOp",EDGE,"E14.left")])]}),makeQuery(id+"F8.opExtrude","SWEPT_FACE",FACE,{"disambiguationData":[OSD([subQ0])]})]}),makeQuery(id+"F10.opExtrude","SWEPT_FACE",FACE,{"disambiguationData":[OSD([sQuery(id+"F9.wireOp",EDGE,"E32.left")])]})]}),makeQuery(id+"F14.opExtrude","SWEPT_FACE",FACE,{"disambiguationData":[OSD([subQ0])]})]});}
            var sketch = newSketch(context, id + "F15", { "sketchPlane" : qUnion([Q0])});
            skCircle(sketch, "E39", {"center": v(-10, 6) * mm, "radius": 1.35 * mm});
            skSolve(sketch);
        }
        {
            var Q0;
            Q0=makeQuery(id+"F15.imprint","IMPRINT",FACE,{"disambiguationData":[TD([[makeQuery(id+"F15.imprint","IMPRINT",EDGE,{"derivedFrom":sQuery(id+"F15.wireOp",EDGE,"E39")}),1.0]])]});
            extrude(context, id + "F16", {"entities" : qUnion([Q0]), "operationType" : NewBodyOperationType.REMOVE, "endBound" : BoundingType.THROUGH_ALL, "oppositeDirection" : true, "depth" : 25 * mm, "offsetDistance" : 25 * mm});
        }
    });
